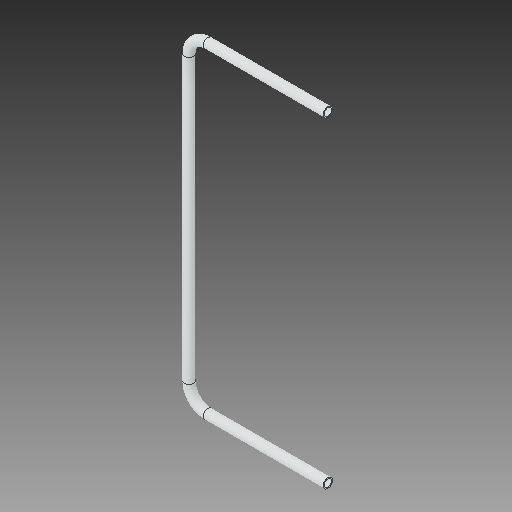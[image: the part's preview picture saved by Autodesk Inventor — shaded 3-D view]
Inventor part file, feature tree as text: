
AUTODESK INVENTOR PART (.ipt)
format: ipt  version: 2018 (Build 220112000, 112)  size: 102,912 bytes
history: native  units: in
note: dims shown in document units (in); Inventor stores cm internally (conversion verified against a paired STEP export)
features: sweep x1
ambient origin geometry x8: Origin, YZ Plane, XZ Plane, XY Plane, X Axis, Y Axis, Z Axis, Center Point
bodies: Solid1 (feature_tree)
feature tree (1):
  sweep  "Sweep1"
